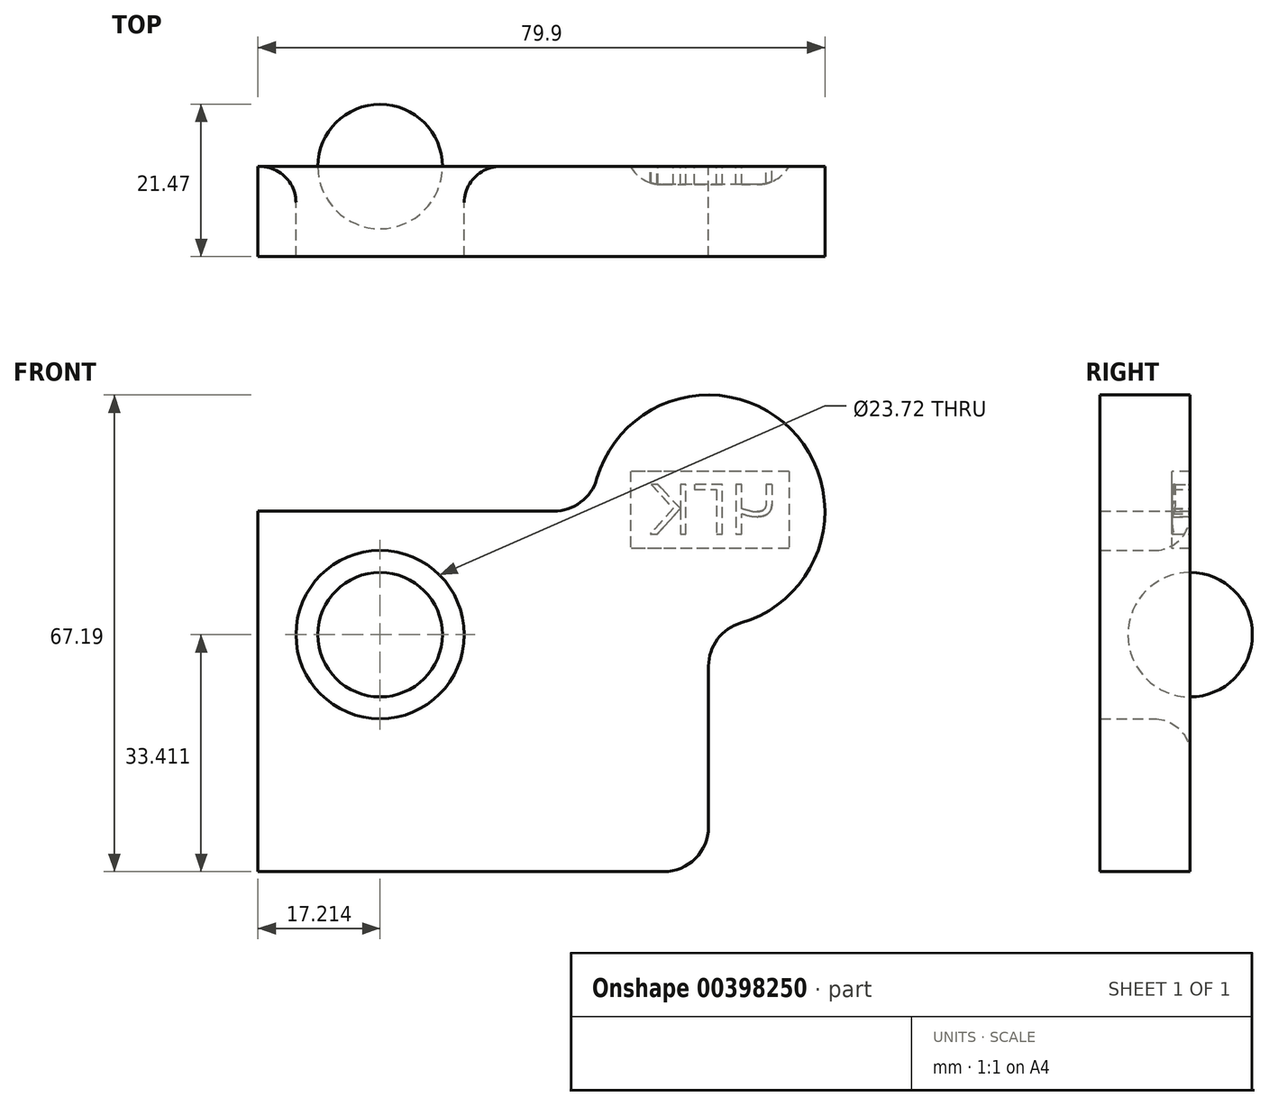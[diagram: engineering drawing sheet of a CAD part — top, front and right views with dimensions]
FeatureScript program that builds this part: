
annotation { "Feature Type Name" : "Feature", "Feature Type Description" : "" }
export const myFeature = defineFeature(function(context is Context, id is Id, definition is map)
    precondition{}
    {
        {
            var Q0;
            Q0=qCreatedBy(makeId("Front.planeOp"),FACE);
            var sketch = newSketch(context, id + "F0", { "sketchPlane" : qUnion([Q0])});
            skLineSegment(sketch, "E0.bottom", {"start": v(-34.25, 31.84) * mm, "end": v(7.41, 31.84) * mm});
            skLineSegment(sketch, "E0.top", {"start": v(-34.25, -18.96) * mm, "end": v(22.9, -18.96) * mm});
            skLineSegment(sketch, "E0.left", {"start": v(-34.25, 31.84) * mm, "end": v(-34.25, -18.96) * mm});
            skLineSegment(sketch, "E0.right", {"start": v(29.25, 10) * mm, "end": v(29.25, -12.61) * mm});
            skArc(sketch, "E1", {"start": v(33.83, 16.1) * mm, "mid": v(40.85, 43.43) * mm, "end": v(13.51, 36.42) * mm});
            skPoint(sketch, "E2.visualSharp", {"position": v(12.86, 31.84) * mm});
            skArc(sketch, "E2.filletArc", {"start": v(7.41, 31.84) * mm, "mid": v(11.23, 33.11) * mm, "end": v(13.51, 36.42) * mm});
            skPoint(sketch, "E3.visualSharp", {"position": v(29.25, 15.44) * mm});
            skArc(sketch, "E3.filletArc", {"start": v(33.83, 16.1) * mm, "mid": v(30.53, 13.81) * mm, "end": v(29.25, 10) * mm});
            skCircle(sketch, "E4", {"center": v(-17.04, 14.45) * mm, "radius": 11.86 * mm});
            skPoint(sketch, "E5.visualSharp", {"position": v(29.25, -18.96) * mm});
            skArc(sketch, "E5.filletArc", {"start": v(22.9, -18.96) * mm, "mid": v(27.4, -17.1) * mm, "end": v(29.25, -12.61) * mm});
            skSolve(sketch);
        }
        {
            var Q0;
            Q0=makeQuery(id+"F0.imprint","IMPRINT",FACE,{"disambiguationData":[TD([[makeQuery(id+"F0.imprint","IMPRINT",EDGE,{"derivedFrom":sQuery(id+"F0.wireOp",EDGE,"E0.bottom")}),-1.0]])]});
            extrude(context, id + "F1", {"entities" : qUnion([Q0]), "depth" : 12.7 * mm});
        }
        {
            var Q0;
            Q0=makeQuery(id+"F1.opExtrude","CAP_FACE",FACE,{"disambiguationData":[OSD([sQuery(id+"F0.wireOp",EDGE,"E0.bottom"),sQuery(id+"F0.wireOp",EDGE,"E0.top"),sQuery(id+"F0.wireOp",EDGE,"E0.left"),sQuery(id+"F0.wireOp",EDGE,"E0.right"),sQuery(id+"F0.wireOp",EDGE,"E1"),sQuery(id+"F0.wireOp",EDGE,"E2.filletArc"),sQuery(id+"F0.wireOp",EDGE,"E3.filletArc"),sQuery(id+"F0.wireOp",EDGE,"E4"),sQuery(id+"F0.wireOp",EDGE,"E5.filletArc")])],"isStart":true});
            var sketch = newSketch(context, id + "F2", { "sketchPlane" : qUnion([Q0])});
            skArc(sketch, "E6", {"start": v(17.04, 23.22) * mm, "mid": v(8.26, 14.45) * mm, "end": v(17.04, 5.68) * mm});
            skLineSegment(sketch, "E7", {"start": v(17.04, 14.45) * mm, "end": v(17.04, 23.22) * mm});
            skLineSegment(sketch, "E8", {"start": v(17.04, 23.22) * mm, "end": v(17.04, 5.68) * mm});
            skSolve(sketch);
        }
        {
            var Q0;
            {var subQ0=sQuery(id+"F2.wireOp",EDGE,"E6");Q0=makeQuery(id+"F2.imprint","IMPRINT",FACE,{"disambiguationData":[TD([[makeQuery(id+"F2.imprint","IMPRINT",EDGE,{"derivedFrom":subQ0}),1.0]])]});}
            var Q1;
            Q1=sQuery(id+"F2.wireOp",EDGE,"E8");
            revolve(context, id + "F3", {"entities" : qUnion([Q0]), "axis" : qUnion([Q1]), "revolveType" : RevolveType.FULL});
        }
        {
            var Q0;
            Q0=makeQuery(id+"F1.opExtrude","CAP_EDGE",EDGE,{"disambiguationData":[OSD([sQuery(id+"F0.wireOp",EDGE,"E4")])],"isStart":true});
            fillet(context, id + "F4", {"entities" : qUnion([Q0]), "radius" : 5.08 * mm, "tangentPropagation" : true, "allowEdgeOverflow" : false});
        }
        {
            var Q0;
            Q0=makeQuery(id+"F1.opExtrude","CAP_FACE",FACE,{"disambiguationData":[OSD([sQuery(id+"F0.wireOp",EDGE,"E0.bottom"),sQuery(id+"F0.wireOp",EDGE,"E0.top"),sQuery(id+"F0.wireOp",EDGE,"E0.left"),sQuery(id+"F0.wireOp",EDGE,"E0.right"),sQuery(id+"F0.wireOp",EDGE,"E1"),sQuery(id+"F0.wireOp",EDGE,"E2.filletArc"),sQuery(id+"F0.wireOp",EDGE,"E3.filletArc"),sQuery(id+"F0.wireOp",EDGE,"E4"),sQuery(id+"F0.wireOp",EDGE,"E5.filletArc")])],"isStart":true});
            var sketch = newSketch(context, id + "F5", { "sketchPlane" : qUnion([Q0])});
            skText(sketch, "E9", { "text": "ЧГК", "fontName": "OpenSans-Regular.ttf"});
            skLineSegment(sketch, "E10.bottom", {"start": v(-40.57, 37.48) * mm, "end": v(-18.23, 37.48) * mm});
            skLineSegment(sketch, "E10.top", {"start": v(-40.57, 26.61) * mm, "end": v(-18.23, 26.61) * mm});
            skLineSegment(sketch, "E10.left", {"start": v(-40.57, 37.48) * mm, "end": v(-40.57, 26.61) * mm});
            skLineSegment(sketch, "E10.right", {"start": v(-18.23, 37.48) * mm, "end": v(-18.23, 26.61) * mm});
            const initialGuessF5  = {"E9": [-0.03899, 0.02861, 1, 0, 0.00708]};
            skSetInitialGuess(sketch, initialGuessF5);
            skSolve(sketch);
        }
        {
            var Q0;
            Q0=makeQuery(id+"F5.imprint","IMPRINT",FACE,{"disambiguationData":[TD([[makeQuery(id+"F5.imprint","IMPRINT",EDGE,{"derivedFrom":sQuery(id+"F5.wireOp",EDGE,"E9.sketch_text.stroke-0")}),1.0]])]});
            extrude(context, id + "F6", {"entities" : qUnion([Q0]), "operationType" : NewBodyOperationType.REMOVE, "oppositeDirection" : true, "depth" : 2.54 * mm});
        }
        {
            var Q0;
            Q0=makeQuery(id+"F6.boolean.opBoolean","COPY",EDGE,{"derivedFrom":makeQuery(id+"F6.opExtrude","CAP_EDGE",EDGE,{"disambiguationData":[OSD([sQuery(id+"F5.wireOp",EDGE,"E10.right")])],"isStart":false})});
            fillet(context, id + "F7", {"entities" : qUnion([Q0]), "radius" : 5.08 * mm, "tangentPropagation" : true, "allowEdgeOverflow" : false});
        }
        {
            var Q0;
            Q0=makeQuery(id+"F6.boolean.opBoolean","COPY",EDGE,{"derivedFrom":makeQuery(id+"F6.opExtrude","CAP_EDGE",EDGE,{"disambiguationData":[OSD([sQuery(id+"F5.wireOp",EDGE,"E10.left")])],"isStart":false})});
            fillet(context, id + "F8", {"entities" : qUnion([Q0]), "radius" : 5.08 * mm, "tangentPropagation" : true, "allowEdgeOverflow" : false});
        }
    });
